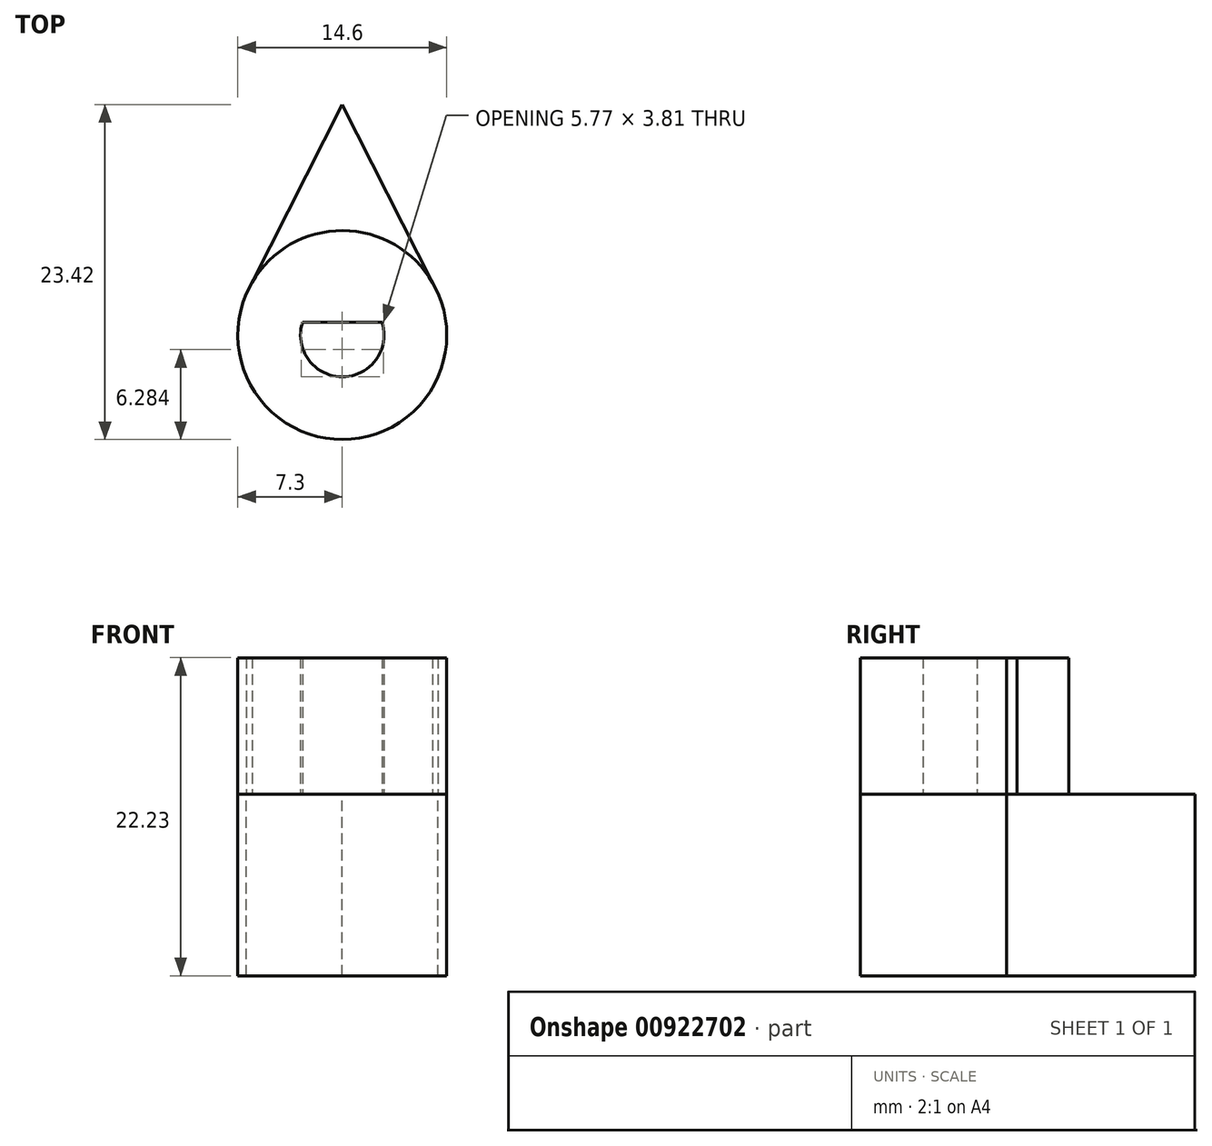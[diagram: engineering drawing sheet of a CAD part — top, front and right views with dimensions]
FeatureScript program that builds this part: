
annotation { "Feature Type Name" : "Feature", "Feature Type Description" : "" }
export const myFeature = defineFeature(function(context is Context, id is Id, definition is map)
    precondition{}
    {
        {
            var Q0;
            Q0=qCreatedBy(makeId("Top.planeOp"),FACE);
            var sketch = newSketch(context, id + "F0", { "sketchPlane" : qUnion([Q0])});
            skCircle(sketch, "E0", {"center": v(0, 0) * mm, "radius": 2.92 * mm});
            skCircle(sketch, "E1", {"center": v(0, 0) * mm, "radius": 7.3 * mm});
            skLineSegment(sketch, "E2", {"start": v(-2.78, 0.89) * mm, "end": v(2.78, 0.89) * mm});
            skPoint(sketch, "E3", {"position": v(0, -2.92) * mm});
            skLineSegment(sketch, "E4", {"start": v(0, 16.12) * mm, "end": v(-6.7, 2.9) * mm});
            skLineSegment(sketch, "E5", {"start": v(0, 16.12) * mm, "end": v(6.69, 2.93) * mm});
            skSolve(sketch);
        }
        {
            var Q0;
            {var subQ5=sQuery(id+"F0.wireOp",EDGE,"E2");var subQ6=sQuery(id+"F0.wireOp",EDGE,"E0");var subQ7=makeQuery(id+"F0.imprint","INTERSECT",VERTEX,{"disambiguationData":[OD(0.0)],"derivedFrom":[subQ6,subQ5]});Q0=makeQuery(id+"F0.imprint","IMPRINT",FACE,{"disambiguationData":[TD([[makeQuery(id+"F0.imprint","IMPRINT",EDGE,{"disambiguationData":[TD([[subQ7,1.0]])],"derivedFrom":subQ6}),-1.0]])]});}
            var Q1;
            {var subQ0=sQuery(id+"F0.wireOp",EDGE,"E2");Q1=makeQuery(id+"F0.imprint","IMPRINT",FACE,{"disambiguationData":[TD([[makeQuery(id+"F0.imprint","IMPRINT",EDGE,{"derivedFrom":subQ0}),1.0]])]});}
            extrude(context, id + "F1", {"entities" : qUnion([Q0, Q1]), "depth" : 9.52 * mm, "offsetDistance" : 25.4 * mm});
        }
        {
            var Q0;
            {var subQ0=sQuery(id+"F0.wireOp",EDGE,"E2");Q0=makeQuery(id+"F0.imprint","IMPRINT",FACE,{"disambiguationData":[TD([[makeQuery(id+"F0.imprint","IMPRINT",EDGE,{"derivedFrom":subQ0}),1.0]])]});}
            var Q1;
            {var subQ0=sQuery(id+"F0.wireOp",EDGE,"E2");Q1=makeQuery(id+"F0.imprint","IMPRINT",FACE,{"disambiguationData":[TD([[makeQuery(id+"F0.imprint","IMPRINT",EDGE,{"derivedFrom":subQ0}),-1.0]])]});}
            var Q2;
            {var subQ0=sQuery(id+"F0.wireOp",EDGE,"E5");var subQ1=sQuery(id+"F0.wireOp",EDGE,"E1");var subQ2=makeQuery(id+"F0.imprint","INTERSECT",VERTEX,{"disambiguationData":[OD(1.0)],"derivedFrom":[subQ1,subQ0]});Q2=makeQuery(id+"F0.imprint","IMPRINT",FACE,{"disambiguationData":[TD([[makeQuery(id+"F0.imprint","IMPRINT",EDGE,{"disambiguationData":[TD([[subQ2,-1.0]])],"derivedFrom":subQ1}),-1.0]])]});}
            var Q3;
            {var subQ5=sQuery(id+"F0.wireOp",EDGE,"E2");var subQ6=sQuery(id+"F0.wireOp",EDGE,"E0");var subQ7=makeQuery(id+"F0.imprint","INTERSECT",VERTEX,{"disambiguationData":[OD(0.0)],"derivedFrom":[subQ6,subQ5]});Q3=makeQuery(id+"F0.imprint","IMPRINT",FACE,{"disambiguationData":[TD([[makeQuery(id+"F0.imprint","IMPRINT",EDGE,{"disambiguationData":[TD([[subQ7,1.0]])],"derivedFrom":subQ6}),-1.0]])]});}
            extrude(context, id + "F2", {"entities" : qUnion([Q0, Q1, Q2, Q3]), "depth" : -12.7 * mm, "offsetDistance" : 25.4 * mm});
        }
    });
